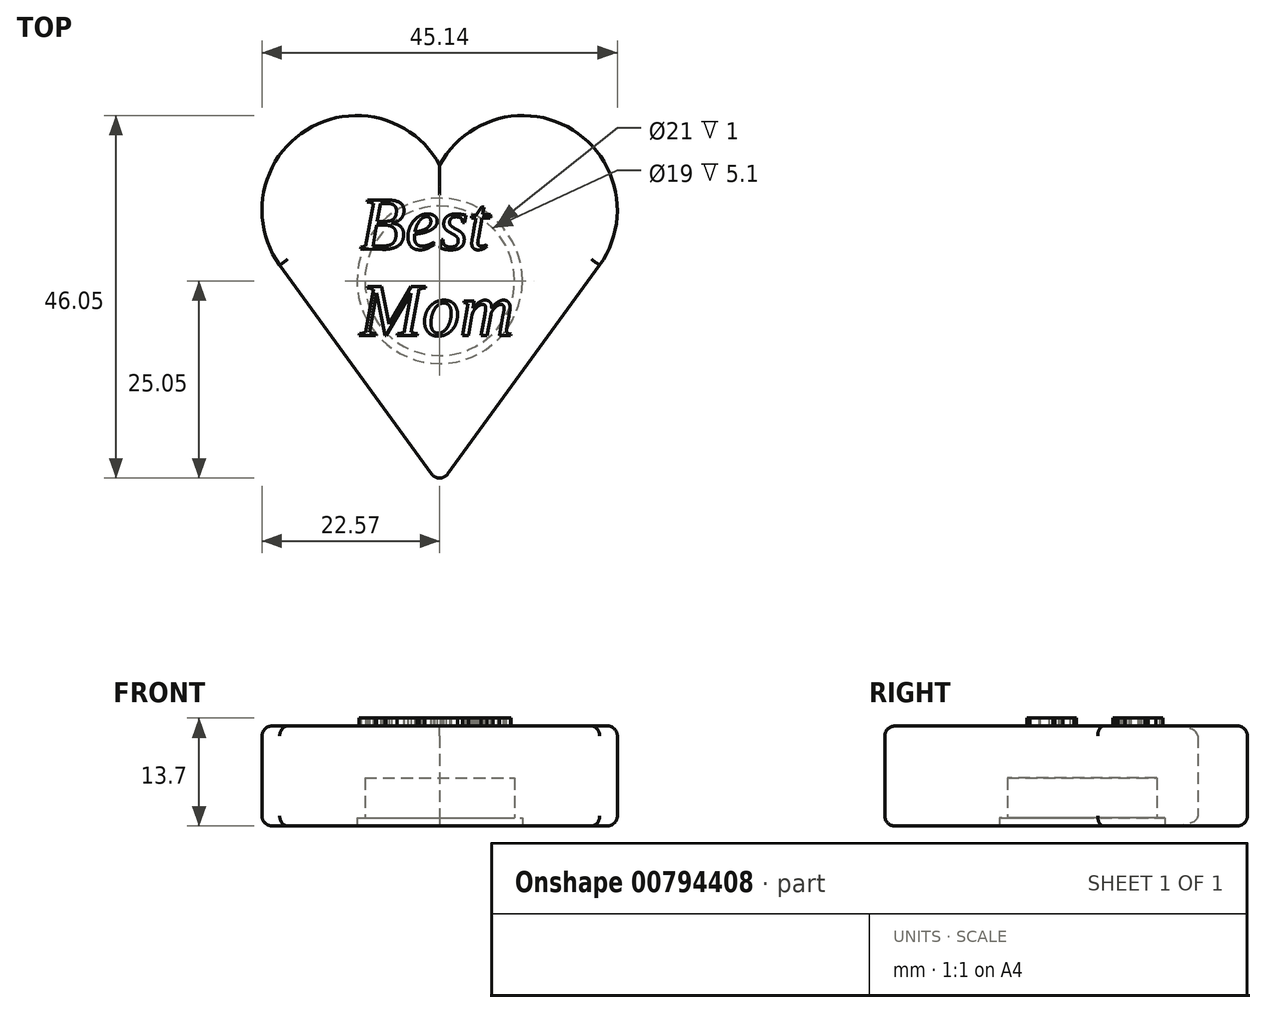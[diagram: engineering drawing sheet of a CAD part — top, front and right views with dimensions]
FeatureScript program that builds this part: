
annotation { "Feature Type Name" : "Feature", "Feature Type Description" : "" }
export const myFeature = defineFeature(function(context is Context, id is Id, definition is map)
    precondition{}
    {
        {
            var Q0;
            Q0=qCreatedBy(makeId("Top.planeOp"),FACE);
            var sketch = newSketch(context, id + "F0", { "sketchPlane" : qUnion([Q0])});
            skLineSegment(sketch, "E0", {"start": v(0, 12.7) * mm, "end": v(0, -27.94) * mm});
            skLineSegment(sketch, "E1", {"start": v(0, 12.7) * mm, "end": v(0, 0) * mm});
            skLineSegment(sketch, "E2", {"start": v(0, 0) * mm, "end": v(0, -27.94) * mm});
            skLineSegment(sketch, "E3", {"start": v(0, 0) * mm, "end": v(-20.32, 0) * mm});
            skLineSegment(sketch, "E4", {"start": v(0, 0) * mm, "end": v(20.32, 0) * mm});
            skLineSegment(sketch, "E5", {"start": v(0, 0) * mm, "end": v(-13.11, 18.73) * mm});
            skLineSegment(sketch, "E6", {"start": v(0, 0) * mm, "end": v(13.11, 18.73) * mm});
            skArc(sketch, "E7", {"start": v(0, 12.7) * mm, "mid": v(-16.93, 17.17) * mm, "end": v(-20.32, 0) * mm});
            skArc(sketch, "E8", {"start": v(20.32, 0) * mm, "mid": v(16.93, 17.17) * mm, "end": v(0, 12.7) * mm});
            skLineSegment(sketch, "E9", {"start": v(-20.32, 0) * mm, "end": v(0, -27.94) * mm});
            skLineSegment(sketch, "E10", {"start": v(0, -27.94) * mm, "end": v(20.32, 0) * mm});
            skSolve(sketch);
        }
        {
            var Q0;
            {var subQ0=sQuery(id+"F0.wireOp",EDGE,"E3");Q0=makeQuery(id+"F0.imprint","IMPRINT",FACE,{"disambiguationData":[TD([[makeQuery(id+"F0.imprint","IMPRINT",EDGE,{"derivedFrom":subQ0}),1.0]])]});}
            var Q1;
            {var subQ0=sQuery(id+"F0.wireOp",EDGE,"E3");Q1=makeQuery(id+"F0.imprint","IMPRINT",FACE,{"disambiguationData":[TD([[makeQuery(id+"F0.imprint","IMPRINT",EDGE,{"derivedFrom":subQ0}),-1.0]])]});}
            var Q2;
            {var subQ0=sQuery(id+"F0.wireOp",EDGE,"E5");Q2=makeQuery(id+"F0.imprint","IMPRINT",FACE,{"disambiguationData":[TD([[makeQuery(id+"F0.imprint","IMPRINT",EDGE,{"derivedFrom":subQ0}),-1.0]])]});}
            var Q3;
            {var subQ0=sQuery(id+"F0.wireOp",EDGE,"E6");Q3=makeQuery(id+"F0.imprint","IMPRINT",FACE,{"disambiguationData":[TD([[makeQuery(id+"F0.imprint","IMPRINT",EDGE,{"derivedFrom":subQ0}),1.0]])]});}
            var Q4;
            {var subQ0=sQuery(id+"F0.wireOp",EDGE,"E4");Q4=makeQuery(id+"F0.imprint","IMPRINT",FACE,{"disambiguationData":[TD([[makeQuery(id+"F0.imprint","IMPRINT",EDGE,{"derivedFrom":subQ0}),1.0]])]});}
            var Q5;
            {var subQ0=sQuery(id+"F0.wireOp",EDGE,"E4");Q5=makeQuery(id+"F0.imprint","IMPRINT",FACE,{"disambiguationData":[TD([[makeQuery(id+"F0.imprint","IMPRINT",EDGE,{"derivedFrom":subQ0}),-1.0]])]});}
            extrude(context, id + "F1", {"entities" : qUnion([Q0, Q1, Q2, Q3, Q4, Q5]), "depth" : 12.7 * mm, "offsetDistance" : 25.4 * mm});
        }
        {
            var Q0;
            Q0=makeQuery(id+"F1.opExtrude","SWEPT_EDGE",EDGE,{"disambiguationData":[OSD([sQuery(id+"F0.wireOp",EDGE,"E0"),sQuery(id+"F0.wireOp",EDGE,"E9"),sQuery(id+"F0.wireOp",EDGE,"E10")])]});
            fillet(context, id + "F2", {"entities" : qUnion([Q0]), "radius" : 1.27 * mm, "tangentPropagation" : true, "allowEdgeOverflow" : false});
        }
        {
            var Q0;
            Q0=makeQuery(id+"FvrJ4b0HHgiXndV_1.boolean.opBoolean","COPY",EDGE,{"derivedFrom":makeQuery(id+"FvrJ4b0HHgiXndV_1.opExtrude","CAP_EDGE",EDGE,{"disambiguationData":[OSD([sQuery(id+"FYHbhXpBtmTDR8c_1.wireOp",EDGE,"EBRQw1Fj-7laH-qRZ9-cXpS-xf0bU6UVibkJ")])],"isStart":true})});
            var Q1;
            Q1=makeQuery(id+"FygZ7wc3xrayfmZ_1.opExtrude","CAP_EDGE",EDGE,{"disambiguationData":[OSD([sQuery(id+"F7mfoubQkbQMzz5_1.wireOp",EDGE,"CQ8zoGXI-2unq-7C4y-x8PT-jk6arYvEebqi.top")])],"isStart":false});
            var Q2;
            Q2=makeQuery(id+"F1.opExtrude","CAP_EDGE",EDGE,{"disambiguationData":[OSD([sQuery(id+"F0.wireOp",EDGE,"E9")])],"isStart":false});
            var Q3;
            Q3=makeQuery(id+"F1.opExtrude","CAP_EDGE",EDGE,{"disambiguationData":[OSD([sQuery(id+"F0.wireOp",EDGE,"E10")])],"isStart":true});
            fillet(context, id + "F3", {"entities" : qUnion([Q0, Q1, Q2, Q3]), "radius" : 1.27 * mm, "tangentPropagation" : true, "allowEdgeOverflow" : false});
        }
        {
            var Q0;
            Q0=makeQuery(id+"F1.opExtrude","CAP_EDGE",EDGE,{"disambiguationData":[OSD([sQuery(id+"F0.wireOp",EDGE,"E7")])],"isStart":false});
            var Q1;
            Q1=makeQuery(id+"F1.opExtrude","CAP_EDGE",EDGE,{"disambiguationData":[OSD([sQuery(id+"F0.wireOp",EDGE,"E8")])],"isStart":false});
            fillet(context, id + "F4", {"entities" : qUnion([Q0, Q1]), "radius" : 1.27 * mm, "tangentPropagation" : true, "allowEdgeOverflow" : false});
        }
        {
            var Q0;
            Q0=makeQuery(id+"F1.opExtrude","CAP_FACE",FACE,{"disambiguationData":[OSD([sQuery(id+"F0.wireOp",EDGE,"E7"),sQuery(id+"F0.wireOp",EDGE,"E8"),sQuery(id+"F0.wireOp",EDGE,"E9"),sQuery(id+"F0.wireOp",EDGE,"E10")])],"isStart":false});
            var sketch = newSketch(context, id + "F5", { "sketchPlane" : qUnion([Q0])});
            skText(sketch, "E11", { "text": "Best\nMom", "fontName": "Tinos-Italic.ttf"});
            const initialGuessF5  = {"E11": [-0.01014, 0.00202, 1, 0, 0.00686]};
            skSetInitialGuess(sketch, initialGuessF5);
            skSolve(sketch);
        }
        {
            var Q0;
            Q0=makeQuery(id+"F5.imprint","IMPRINT",FACE,{"disambiguationData":[TD([[makeQuery(id+"F5.imprint","IMPRINT",EDGE,{"derivedFrom":sQuery(id+"F5.wireOp",EDGE,"E11.sketch_text.stroke-0")}),-1.0]])]});
            var Q1;
            Q1=makeQuery(id+"F5.imprint","IMPRINT",FACE,{"disambiguationData":[TD([[makeQuery(id+"F5.imprint","IMPRINT",EDGE,{"derivedFrom":sQuery(id+"F5.wireOp",EDGE,"E11.sketch_text.stroke-29")}),-1.0]])]});
            var Q2;
            Q2=makeQuery(id+"F5.imprint","IMPRINT",FACE,{"disambiguationData":[TD([[makeQuery(id+"F5.imprint","IMPRINT",EDGE,{"derivedFrom":sQuery(id+"F5.wireOp",EDGE,"E11.sketch_text.stroke-53")}),-1.0]])]});
            var Q3;
            Q3=makeQuery(id+"F5.imprint","IMPRINT",FACE,{"disambiguationData":[TD([[makeQuery(id+"F5.imprint","IMPRINT",EDGE,{"derivedFrom":sQuery(id+"F5.wireOp",EDGE,"E11.sketch_text.stroke-79")}),-1.0]])]});
            var Q4;
            Q4=makeQuery(id+"F5.imprint","IMPRINT",FACE,{"disambiguationData":[TD([[makeQuery(id+"F5.imprint","IMPRINT",EDGE,{"derivedFrom":sQuery(id+"F5.wireOp",EDGE,"E11.sketch_text.stroke-99")}),-1.0]])]});
            var Q5;
            Q5=makeQuery(id+"F5.imprint","IMPRINT",FACE,{"disambiguationData":[TD([[makeQuery(id+"F5.imprint","IMPRINT",EDGE,{"derivedFrom":sQuery(id+"F5.wireOp",EDGE,"E11.sketch_text.stroke-124")}),-1.0]])]});
            var Q6;
            Q6=makeQuery(id+"F5.imprint","IMPRINT",FACE,{"disambiguationData":[TD([[makeQuery(id+"F5.imprint","IMPRINT",EDGE,{"derivedFrom":sQuery(id+"F5.wireOp",EDGE,"E11.sketch_text.stroke-144")}),-1.0]])]});
            extrude(context, id + "F6", {"entities" : qUnion([Q0, Q1, Q2, Q3, Q4, Q5, Q6]), "operationType" : NewBodyOperationType.ADD, "depth" : 1 * mm, "offsetDistance" : 25.4 * mm});
        }
        {
            var Q0;
            Q0=makeQuery(id+"F1.opExtrude","CAP_FACE",FACE,{"disambiguationData":[OSD([sQuery(id+"F0.wireOp",EDGE,"E7"),sQuery(id+"F0.wireOp",EDGE,"E8"),sQuery(id+"F0.wireOp",EDGE,"E9"),sQuery(id+"F0.wireOp",EDGE,"E10")])],"isStart":true});
            var sketch = newSketch(context, id + "F7", { "sketchPlane" : qUnion([Q0])});
            skLineSegment(sketch, "E12", {"start": v(0, 0) * mm, "end": v(0, 2) * mm, "construction": true});
            skCircle(sketch, "E13", {"center": v(0, 2) * mm, "radius": 9.5 * mm});
            skCircle(sketch, "E14", {"center": v(0, 2) * mm, "radius": 2.88 * mm});
            skCircle(sketch, "E15", {"center": v(0, 2) * mm, "radius": 10.5 * mm});
            skSolve(sketch);
        }
        {
            var Q0;
            Q0=makeQuery(id+"F7.imprint","IMPRINT",FACE,{"disambiguationData":[TD([[makeQuery(id+"F7.imprint","IMPRINT",EDGE,{"derivedFrom":sQuery(id+"F7.wireOp",EDGE,"E13")}),-1.0]])]});
            extrude(context, id + "F8", {"entities" : qUnion([Q0]), "operationType" : NewBodyOperationType.REMOVE, "oppositeDirection" : true, "depth" : 1 * mm, "offsetDistance" : 25 * mm});
        }
        {
            var Q0;
            Q0=makeQuery(id+"F7.imprint","IMPRINT",FACE,{"disambiguationData":[TD([[makeQuery(id+"F7.imprint","IMPRINT",EDGE,{"derivedFrom":sQuery(id+"F7.wireOp",EDGE,"E13")}),1.0]])]});
            var Q1;
            Q1=makeQuery(id+"F7.imprint","IMPRINT",FACE,{"disambiguationData":[TD([[makeQuery(id+"F7.imprint","IMPRINT",EDGE,{"derivedFrom":sQuery(id+"F7.wireOp",EDGE,"E14")}),1.0]])]});
            extrude(context, id + "F9", {"entities" : qUnion([Q0, Q1]), "operationType" : NewBodyOperationType.REMOVE, "oppositeDirection" : true, "depth" : 6.1 * mm, "offsetDistance" : 25 * mm});
        }
    });
